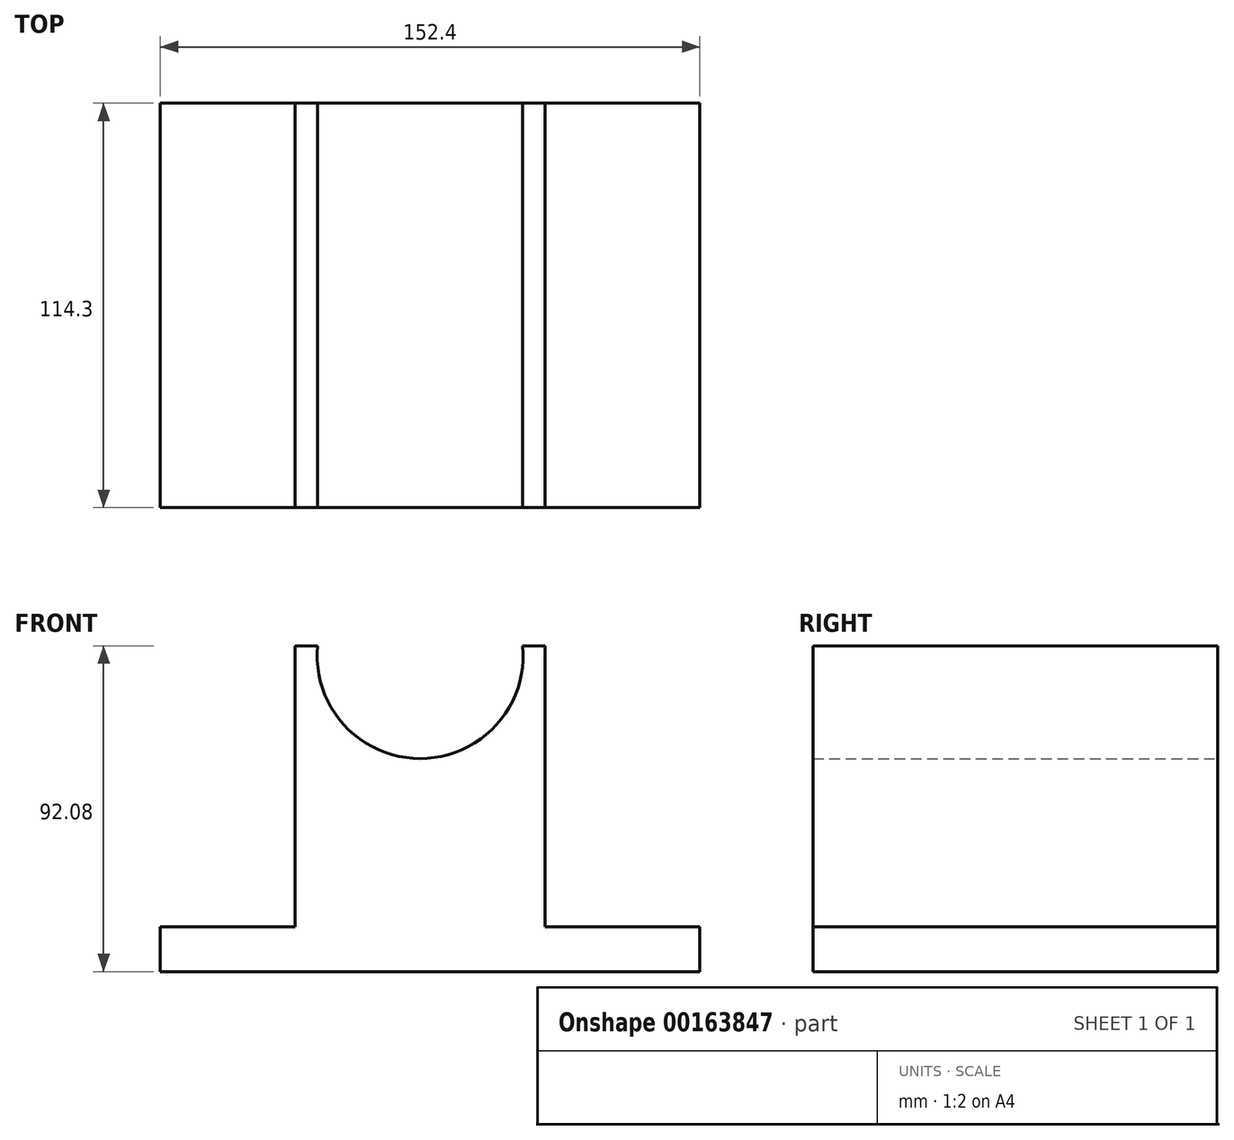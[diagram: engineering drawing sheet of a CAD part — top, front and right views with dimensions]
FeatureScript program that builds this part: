
annotation { "Feature Type Name" : "Feature", "Feature Type Description" : "" }
export const myFeature = defineFeature(function(context is Context, id is Id, definition is map)
    precondition{}
    {
        {
            var Q0;
            Q0=qCreatedBy(makeId("Front.planeOp"),FACE);
            var sketch = newSketch(context, id + "F0", { "sketchPlane" : qUnion([Q0])});
            skLineSegment(sketch, "E0", {"start": v(0, 0) * mm, "end": v(152.4, 0) * mm});
            skLineSegment(sketch, "E1", {"start": v(152.4, 12.7) * mm, "end": v(152.4, 0) * mm});
            skLineSegment(sketch, "E2", {"start": v(0, 0) * mm, "end": v(0, 12.7) * mm});
            skLineSegment(sketch, "E3", {"start": v(38.1, 12.7) * mm, "end": v(0, 12.7) * mm});
            skLineSegment(sketch, "E4", {"start": v(152.4, 12.7) * mm, "end": v(108.72, 12.7) * mm});
            skLineSegment(sketch, "E5", {"start": v(38.1, 12.7) * mm, "end": v(38.1, 92.08) * mm});
            skLineSegment(sketch, "E6", {"start": v(108.72, 92.08) * mm, "end": v(108.72, 12.7) * mm});
            skLineSegment(sketch, "E7", {"start": v(38.1, 92.07) * mm, "end": v(44.45, 92.07) * mm});
            skLineSegment(sketch, "E8", {"start": v(108.72, 92.07) * mm, "end": v(102.37, 92.07) * mm});
            skArc(sketch, "E9", {"start": v(44.45, 92.07) * mm, "mid": v(73.4, 60.2) * mm, "end": v(102.37, 92.07) * mm});
            skSolve(sketch);
        }
        {
            var Q0;
            Q0=makeQuery(id+"F0.imprint","IMPRINT",FACE,{"disambiguationData":[TD([[makeQuery(id+"F0.imprint","IMPRINT",EDGE,{"derivedFrom":sQuery(id+"F0.wireOp",EDGE,"E0")}),1.0]])]});
            extrude(context, id + "F1", {"entities" : qUnion([Q0]), "depth" : 25.4 * mm});
        }
        {
            var Q0;
            Q0=makeQuery(id+"F0.imprint","IMPRINT",FACE,{"disambiguationData":[TD([[makeQuery(id+"F0.imprint","IMPRINT",EDGE,{"derivedFrom":sQuery(id+"F0.wireOp",EDGE,"E0")}),1.0]])]});
            extrude(context, id + "F2", {"entities" : qUnion([Q0]), "operationType" : NewBodyOperationType.ADD, "depth" : 114.3 * mm});
        }
    });
